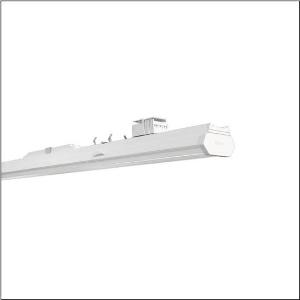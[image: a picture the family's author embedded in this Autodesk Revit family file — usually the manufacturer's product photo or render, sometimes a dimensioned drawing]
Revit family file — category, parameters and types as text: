
# Revit family: licross_r__21_protected_mo_52td1b7n48xg_600d
name_source: partatom
category: Lighting Fixtures
units: mm (PartAtom-declared; Revit-internal decimal feet)

## family parameters
Cut with Voids When Loaded = No
Host = Face
Light Source = No
Part Type = Normal
Room Calculation Point = No
Round Connector Dimension = Use Diameter
Shared = No

## types (1)
- Licross® 21 Protected MO (1 x LED, 8090 lm, 47.9 W, 4000K)
    Apparent Load = 48 VA
    CIE Flux Codes = 54 82 95 97 100
    Color Rendering = 80
    Color Temperature = 4000K
    Default Elevation = 1800 mm
    Description = Licross® 21 Protected MO, luminaire insert, of sheet steel, galvanised, coil coated, white, length: 1.500mm, width: 90mm, height: 103mm, LED rated luminous flux: 8.090lm, light colour: 840, SDCM (Standard Deviation of Colour Matching)MacAdam ≤ 3 SDCM (initial), control gear: ON/OFF, with plug, 3-pole, with phase selection, mains connection: 220..240V, AC, 50/60Hz, rated input power: 48W, internal wiring halogen-free, primary optical cover: cover, of PMMA, light emission: direct distribution, primary light characteristic: symmetric, protection rating (complete): IP54, insulation class (complete): insulation class I (protective earthing), certification: CE, ENEC, VDE, UKCA, protection symbol: D if used in an environment with non-conductive dust loads with corresponding accessories, impact resistance: IK06, permissible ambient temperature for indoor applications: -35..+45°C, corresponds to IFS (International Featured Standards) requirements for safety and quality in the food industry, reducing of maximum allowable ambient temperature of 5°C with ceiling mounting, LABS conformity tested according to VDMA 24364:2018-05, packaging unit: 1 piece
    Height = 92 mm
    Lamp = 1 x LED
    Lamp Light Flux = 8090 lm
    Lamp Power = 47.9 W
    Lamp count = 1
    Length = 1500 mm
    Luminous efficacy = 169 lm/W
    Manufacturer = Siteco
    ModVariant = No
    Model = 52TD1B7N48XG
    Mounting Place = Ceiling
    Mounting Type = Pendant
    Number of Poles = 1
    OnlyDefault = Yes
    Power Factor = 1
    Product Name = Licross® 21 Protected MO
    Product group = luminaire insert | ceiling pendant
    ProductGroupID = 901
    Protection Class = Protection class I
    Protection Degree = IP 54
    RLX_Detail_Level = 1
    RLX_Emergency_Light_Flux = 0 lm
    RLX_Emergency_Type = 0
    RLX_Emergency_Type_DB = No
    RlxData = <blob elided: 20777 chars, md5=baaa52f2>
    Socket = socket
    Standby Power = 0 W
    System Light Flux = 8090 lm
    System Power = 48 W
    Type Comments = Product without accessories
    Type Image = l_1256148.jpg
    URL = http://relux.com
    VarID = ---
    Voltage = 0 V
    Weight = 0.00 kg
    Width = 88 mm

## geometry (parser evidence)
native form markers: Blend x4, Sweep x10
no freeform markers — native parametric forms only
